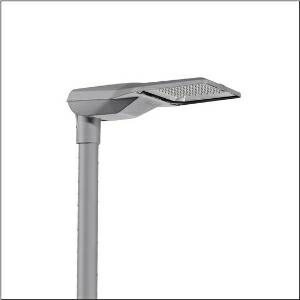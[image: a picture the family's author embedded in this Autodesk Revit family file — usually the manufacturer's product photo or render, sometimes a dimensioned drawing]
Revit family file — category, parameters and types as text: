
# Revit family: streetlight_sl_21_midi___st1_0ab_5xe7m33a08lb_7eb4
name_source: partatom
category: Lighting Fixtures
units: mm (PartAtom-declared; Revit-internal decimal feet)

## family parameters
Cut with Voids When Loaded = No
Host = Face
Light Source = No
Part Type = Normal
Room Calculation Point = No
Round Connector Dimension = Use Diameter
Shared = No

## types (1)
- --- (1 x LED, 12620 lm, 98.3 W, 3000K)
    Apparent Load = 98 VA
    CIE Flux Codes = 38 73 97 100 100
    Color Rendering = 70
    Color Temperature = 3000K
    Default Elevation = 1800 mm
    Description = Streetlight SL 21 midi, mast luminaire, primary light control with lens, of PMMA, primary optical cover: cover, of toughened safety glass, transparent, light distribution: ST1.0aB, light emission: direct distribution, primary light characteristic: asymmetric, installation type: post-top, side-entry, LED, 3G 1.5mm², High Power LED, rated luminous flux: 12.620lm, luminous efficacy: 128lm/W, light colour: 730, colour temperature: 3000K, control gear: Easy, control: flexible luminous flux parameterisation, time-dependent luminous flux control, constant luminous flux control, overheat protection, mains connection: 220..240V, AC, 50/60Hz, connection cable pre-assembled, cable length: 10,5m, wiring characteristics: H07RN-F, start of lifetime: 98W, end of service life: 101W, reduction: 44W, luminaire housing, of diecast aluminium, powder-coated, Siteco® metallic grey (DB 702S), corrosivity category C5 mid according to DIN EN ISO 12944, please order mast flange separately, inclination adjustable: 0°, 5°, 10°, 15°, sealing non-destructively replaceable, multi-level sealing system, length: 644mm, width: 335mm, height: 110mm, mast flange for spigot size: 42mm (side-entry): 5XC10008XM4, 60/48mm (side-entry/post-top): 5XC10108XM2, 76/60mm (side-entry/post-top): 5XC10108XM1, mounting height: 4..8m, protection rating (complete): IP66, insulation class (complete): insulation class II (safety insulation), certification: CE, ENEC, ENEC+, VDE, impact resistance: IK10, permissible operating ambient temperature for outdoor applications: -40..+50°C, standard-compliant lighting for roads and squares, packaging unit: 1 piece

Light Distribution: ST1.0aB
    Height = 111 mm
    Lamp = 1 x LED
    Lamp Light Flux = 12620 lm
    Lamp Power = 98.3 W
    Lamp count = 1
    Length = 644 mm
    Luminous efficacy = 128 lm/W
    Manufacturer = Siteco
    ModVariant = No
    Model = 5XE7M33A08LB
    Number of Poles = 1
    OnlyDefault = Yes
    Power Factor = 1
    Product Name = Streetlight SL 21 midi | ST1.0aB
    Product group = mast luminaire | pylon top
    ProductGroupID = 6100
    Protection Class = Protection class II
    Protection Degree = IP 66
    RLX_Detail_Level = 1
    RLX_Emergency_Light_Flux = 0 lm
    RLX_Emergency_Type = 0
    RLX_Emergency_Type_DB = No
    RlxData = <blob elided: 26833 chars, md5=c8a88901>
    Socket = socket
    Standby Power = 0 W
    System Light Flux = 12620 lm
    System Power = 98 W
    Type Comments = factory setting: luminous flux: 100 % | Output Level: 100 % | 1020 mA
    Type Image = l_1004298.jpg
    URL = http://relux.com
    VarID = @adj_204143
    Voltage = 0 V
    Weight = 0.00 kg
    Width = 336 mm

## geometry (parser evidence)
native form markers: Blend x4, Sweep x10
no freeform markers — native parametric forms only
